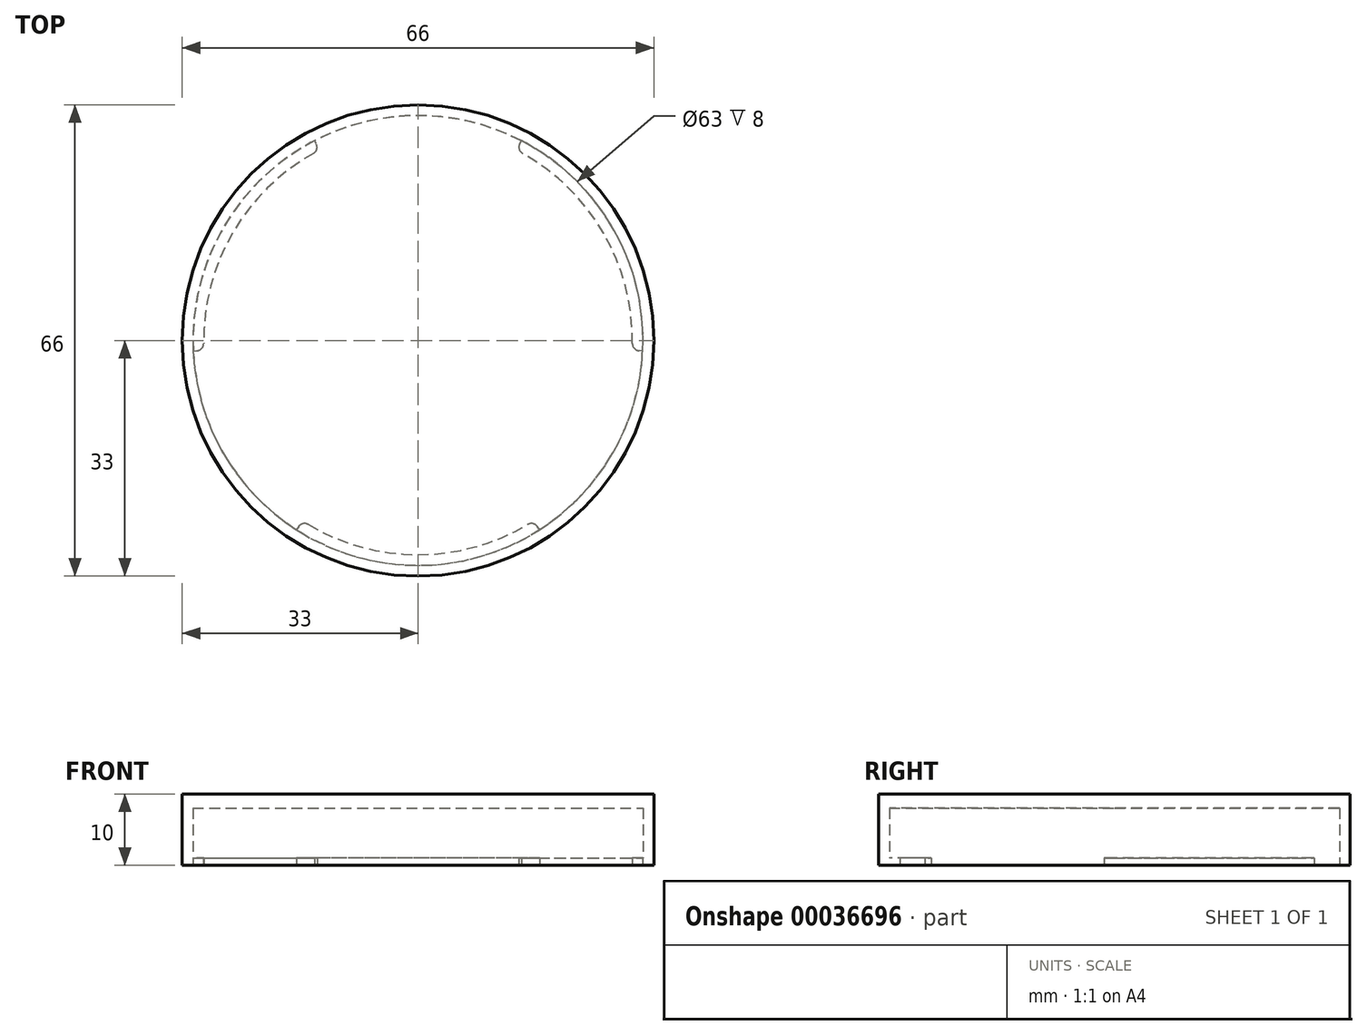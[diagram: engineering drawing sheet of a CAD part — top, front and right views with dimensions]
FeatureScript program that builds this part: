
annotation { "Feature Type Name" : "Feature", "Feature Type Description" : "" }
export const myFeature = defineFeature(function(context is Context, id is Id, definition is map)
    precondition{}
    {
        {
            var Q0;
            Q0=qCreatedBy(makeId("Top.planeOp"),FACE);
            var sketch = newSketch(context, id + "F0", { "sketchPlane" : qUnion([Q0])});
            skCircle(sketch, "E0", {"center": v(0, 0) * mm, "radius": 33 * mm});
            skSolve(sketch);
        }
        {
            var Q0;
            Q0=makeQuery(id+"F0.imprint","IMPRINT",FACE,{"disambiguationData":[TD([[makeQuery(id+"F0.imprint","IMPRINT",EDGE,{"derivedFrom":sQuery(id+"F0.wireOp",EDGE,"E0")}),1.0]])]});
            extrude(context, id + "F1", {"entities" : qUnion([Q0]), "depth" : 10 * mm});
        }
        {
            var Q0;
            Q0=makeQuery(id+"F1.opExtrude","CAP_FACE",FACE,{"disambiguationData":[OSD([sQuery(id+"F0.wireOp",EDGE,"E0")])],"isStart":true});
            var sketch = newSketch(context, id + "F2", { "sketchPlane" : qUnion([Q0])});
            skCircle(sketch, "E1.0", {"center": v(0, 0) * mm, "radius": 31.5 * mm});
            skSolve(sketch);
        }
        {
            var Q0;
            Q0 = qSketchRegion(id + "F2", true);
            extrude(context, id + "F3", {"entities" : qUnion([Q0]), "operationType" : NewBodyOperationType.REMOVE, "oppositeDirection" : true, "depth" : 8 * mm});
        }
        {
            var Q0;
            Q0=makeQuery(id+"F1.opExtrude","CAP_FACE",FACE,{"disambiguationData":[OSD([sQuery(id+"F0.wireOp",EDGE,"E0")])],"isStart":true});
            var sketch = newSketch(context, id + "F4", { "sketchPlane" : qUnion([Q0])});
            skLineSegment(sketch, "E2", {"start": v(0, 0) * mm, "end": v(0, 31.5) * mm, "construction": true});
            skArc(sketch, "E3.0", {"start": v(17, 26.52) * mm, "mid": v(0, 31.5) * mm, "end": v(-17, 26.52) * mm});
            skArc(sketch, "E4.0", {"start": v(16.2, 25.26) * mm, "mid": v(0, 30) * mm, "end": v(-16.2, 25.26) * mm});
            skLineSegment(sketch, "E5", {"start": v(-16.2, 25.26) * mm, "end": v(-17, 26.52) * mm});
            skLineSegment(sketch, "E6", {"start": v(17, 26.52) * mm, "end": v(16.2, 25.26) * mm});
            skLineSegment(sketch, "E7", {"start": v(0, 0) * mm, "end": v(-17, 26.52) * mm, "construction": true});
            skLineSegment(sketch, "E8", {"start": v(0, 0) * mm, "end": v(17, 26.52) * mm, "construction": true});
            skArc(sketch, "E9.1.0", {"start": v(-31.47, 1.46) * mm, "mid": v(-27.28, -15.75) * mm, "end": v(-14.47, -27.98) * mm});
            skArc(sketch, "E9.1.1", {"start": v(-29.97, 1.4) * mm, "mid": v(-25.98, -15) * mm, "end": v(-13.78, -26.65) * mm});
            skLineSegment(sketch, "E9.1.2", {"start": v(-13.78, -26.65) * mm, "end": v(-14.47, -27.98) * mm});
            skLineSegment(sketch, "E9.1.3", {"start": v(-31.47, 1.46) * mm, "end": v(-29.97, 1.4) * mm});
            skArc(sketch, "E9.2.0", {"start": v(14.47, -27.98) * mm, "mid": v(27.28, -15.75) * mm, "end": v(31.47, 1.46) * mm});
            skArc(sketch, "E9.2.1", {"start": v(13.78, -26.65) * mm, "mid": v(25.98, -15) * mm, "end": v(29.97, 1.4) * mm});
            skLineSegment(sketch, "E9.2.2", {"start": v(31.47, 1.46) * mm, "end": v(29.97, 1.4) * mm});
            skLineSegment(sketch, "E9.2.3", {"start": v(13.78, -26.65) * mm, "end": v(14.47, -27.98) * mm});
            skSolve(sketch);
        }
        {
            var Q0;
            Q0 = qSketchRegion(id + "F4", true);
            extrude(context, id + "F5", {"entities" : qUnion([Q0]), "operationType" : NewBodyOperationType.ADD, "oppositeDirection" : true, "depth" : 1 * mm});
        }
        {
            var Q0;
            Q0=makeQuery(id+"F5.opExtrude","SWEPT_EDGE",EDGE,{"disambiguationData":[OSD([sQuery(id+"F4.wireOp",EDGE,"E9.2.1"),sQuery(id+"F4.wireOp",EDGE,"E9.2.2")])]});
            var Q1;
            Q1=makeQuery(id+"F5.opExtrude","SWEPT_EDGE",EDGE,{"disambiguationData":[OSD([sQuery(id+"F4.wireOp",EDGE,"E9.2.1"),sQuery(id+"F4.wireOp",EDGE,"E9.2.3")])]});
            var Q2;
            Q2=makeQuery(id+"F5.opExtrude","SWEPT_EDGE",EDGE,{"disambiguationData":[OSD([sQuery(id+"F4.wireOp",EDGE,"E4.0"),sQuery(id+"F4.wireOp",EDGE,"E6")])]});
            var Q3;
            Q3=makeQuery(id+"F5.opExtrude","SWEPT_EDGE",EDGE,{"disambiguationData":[OSD([sQuery(id+"F4.wireOp",EDGE,"E9.1.1"),sQuery(id+"F4.wireOp",EDGE,"E9.1.2")])]});
            var Q4;
            Q4=makeQuery(id+"F5.opExtrude","SWEPT_EDGE",EDGE,{"disambiguationData":[OSD([sQuery(id+"F4.wireOp",EDGE,"E9.1.1"),sQuery(id+"F4.wireOp",EDGE,"E9.1.3")])]});
            var Q5;
            Q5=makeQuery(id+"F5.opExtrude","SWEPT_EDGE",EDGE,{"disambiguationData":[OSD([sQuery(id+"F4.wireOp",EDGE,"E4.0"),sQuery(id+"F4.wireOp",EDGE,"E5")])]});
            fillet(context, id + "F6", {"entities" : qUnion([Q0, Q1, Q2, Q3, Q4, Q5]), "radius" : 1 * mm, "tangentPropagation" : true, "allowEdgeOverflow" : false});
        }
    });
